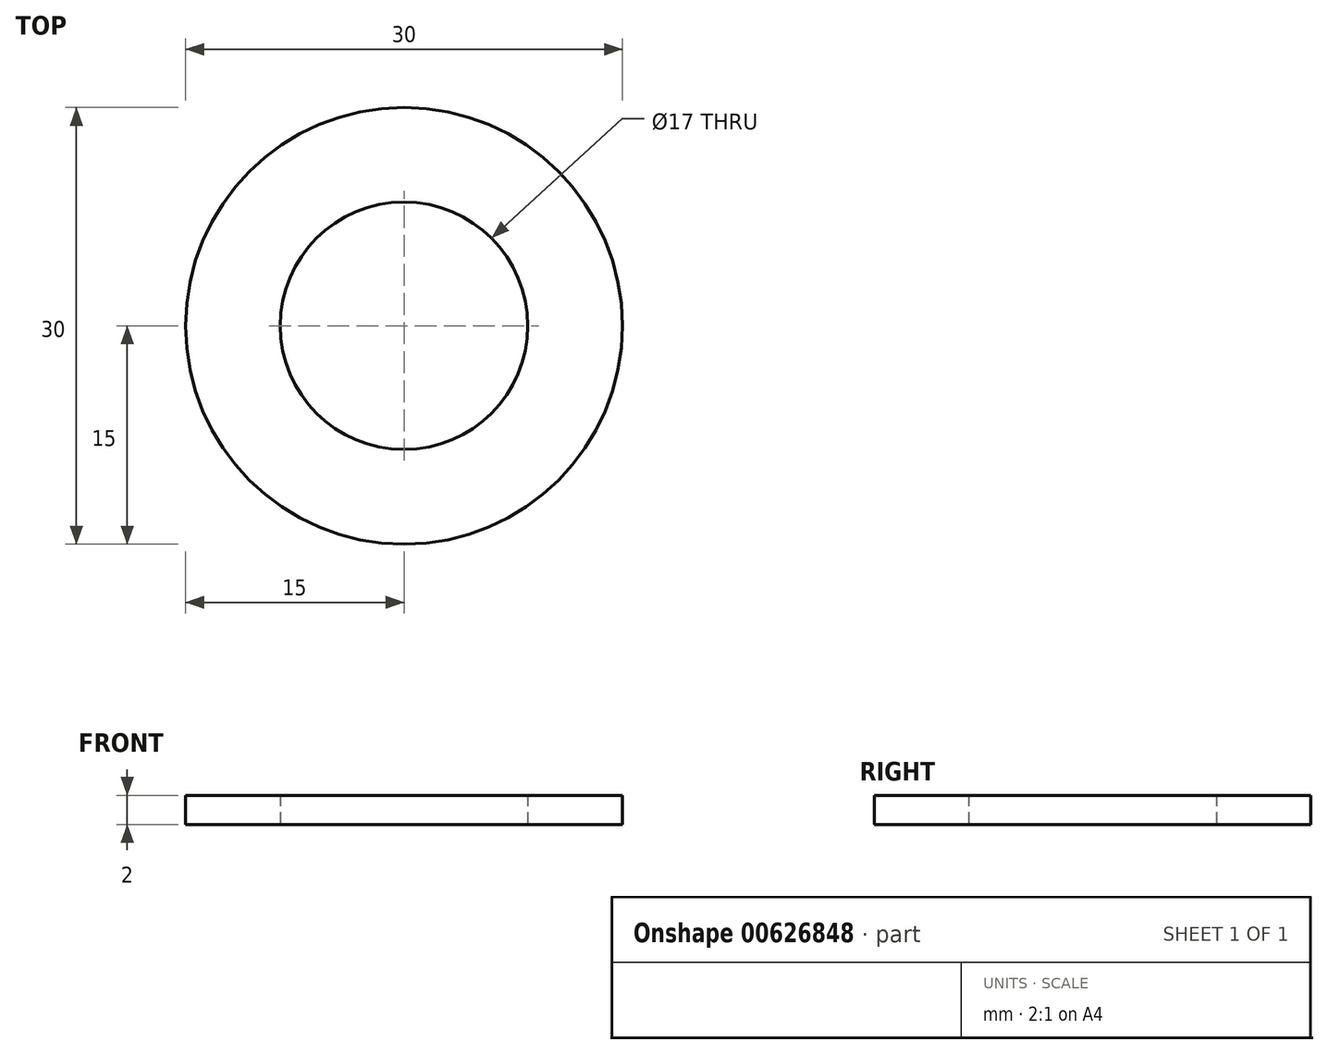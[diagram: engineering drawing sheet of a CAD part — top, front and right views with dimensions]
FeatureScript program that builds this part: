
annotation { "Feature Type Name" : "Feature", "Feature Type Description" : "" }
export const myFeature = defineFeature(function(context is Context, id is Id, definition is map)
    precondition{}
    {
        {
            var Q0;
            Q0=qCreatedBy(makeId("Top.planeOp"),FACE);
            var sketch = newSketch(context, id + "F0", { "sketchPlane" : qUnion([Q0])});
            skCircle(sketch, "E0", {"center": v(0, 0) * mm, "radius": 8.5 * mm});
            skCircle(sketch, "E1", {"center": v(0, 0) * mm, "radius": 15 * mm});
            skSolve(sketch);
        }
        {
            var Q0;
            Q0 = qSketchRegion(id + "F0", true);
            extrude(context, id + "F1", {"entities" : qUnion([Q0]), "depth" : 2 * mm, "offsetDistance" : 25 * mm});
        }
    });
